# Revit family: CW_232-14_Damper-Fire_Round_BRS_01
name_source: partatom
category: Duct Accessories
units: mm (PartAtom-declared; Revit-internal decimal feet)

## family parameters
Always vertical = Yes
Cut with Voids When Loaded = No
Part Type = Damper
Round Connector Dimension = Use Radius
Shared = No
Work Plane-Based = No

## types (1)
- Damper_BRS_Ø160
    Default Elevation = 0 mm  [stored 0 ft]
    Description = BRS
    H2D = 160 mm
    L2D = 235 mm
    MC_R1 = 80 mm
    MC_R2 = 80 mm
    W2D = 160 mm
    concDirPhi1 = 180.00°
    concDirPhi2 = 0.00°
    concDirTheta1 = 90.00°
    concDirTheta2 = 90.00°
    concLocPhi1 = 180.00°
    concLocPhi2 = 0.00°
    concLocR1 = 118 mm
    concLocR2 = 118 mm
    concLocTheta1 = 90.00°
    concLocTheta2 = 90.00°
    magiFamilyGeom = MagiCAD_CR60-160
    magiPartTypeId = 1

note: [stored X ft] marks values corroborated as IEEE doubles in the binary element streams (Revit-internal decimal feet)

## geometry (parser evidence)
native form markers: Sweep x35
no freeform markers — native parametric forms only
